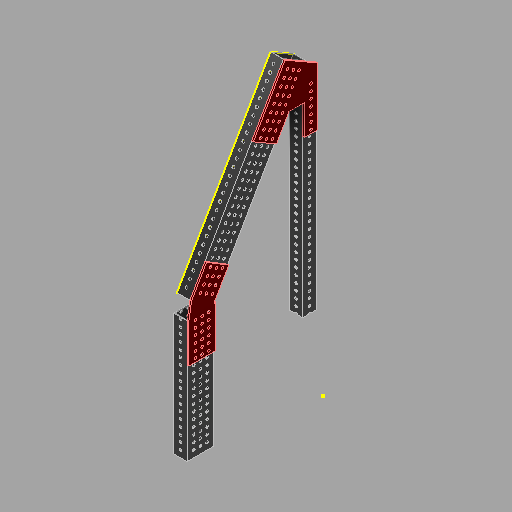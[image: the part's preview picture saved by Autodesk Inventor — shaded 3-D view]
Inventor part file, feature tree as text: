
AUTODESK INVENTOR PART (.ipt)
format: ipt  version: 2024.2 (Build 282272000, 272)  size: 1,339,904 bytes
history: native  units: in
note: dims shown in document units (in); Inventor stores cm internally (conversion verified against a paired STEP export)
features: extrude x12, projected_geometry x11, sketch x10, other x5
ambient origin geometry x8: Origin, YZ Plane, XZ Plane, XY Plane, X Axis, Y Axis, Z Axis, Center Point
bodies: Body1 (feature_tree), Body2 (feature_tree), Body3 (feature_tree), Body4 (feature_tree), Body5 (feature_tree)
feature tree (38):
  other  "2024-210-001-Shooter-Beam"
  sketch  "Sketch1"  dims[d25=9.12in d26=2.0in]
  extrude  "Extrusion1"  Depth=2.0in
  extrude  "Extrusion2"  Depth=2.0in
  extrude  "Extrusion3"  TaperAngle=60.0deg  [1 undecoded]
  extrude  "Extrusion4"  Depth=2.0in
  extrude  "Extrusion5"  Depth=6.654in
  extrude  "Extrusion6"  Depth=2.0in
  sketch  "Sketch5"  dims[d43=1.0in d44=6.654in]
  extrude  "Extrusion7"  Depth=2.0in
  extrude  "Extrusion8"  Depth=0.5in
  extrude  "Extrusion9"  Depth=17.5in
  extrude  "Extrusion10"  Depth=1.0in TaperAngle=0.0deg
  extrude  "Extrusion12"  Depth=1.0in TaperAngle=0.0deg
  extrude  "Extrusion13"  Depth=2.0in
  sketch  "Sketch10"  dims[d71=1.0in d72=0.0in d73=1.0in d74=0.0in d85=1.0in d86=0.0in d87=0.196in d88=0.5in d89=0.5in d90=1.1811in d92=0.5in d93=7.0866in d95=0.5in d98=0.0625in d99=9.5625in d100=0.0in d101=0.0625in d102=9.5625in d103=0.0in d104=0.196in d105=0.5in d106=0.5in d107=13.7795in d109=0.5in d110=0.3937in d112=1.0in d114=0.0625in d115=1.0in d116=0.0in d117=2.87in d118=2.25in d119=2.25in d120=1.5in d122=4.75in d123=0.125in d124=0.0in d125=0.125in d126=0.0in d130=0.196in d131=0.5in d132=0.5in d133=13.7795in d135=0.5in d136=0.3937in d138=1.0in d140=0.125in d141=0.0in d142=0.196in d143=0.5in d144=0.5in d145=10.6299in d147=0.5in d148=0.3937in d150=1.0in d152=1.0in d153=0.0in d166=0.196in d167=0.5in d168=0.5in d169=7.0866in d171=0.5in d172=0.3937in d174=1.0in d176=1.0in d177=0.0in d178=2.0in d179=0.0in d127=0.5in d128=0.0344in]
  other  "2024-210-003-Front-Angle"
  other  "2024-210-002-Backright-Support"
  sketch  "Sketch2"  dims[d29=2.0in d34=0.25in]
  projected_geometry  "Projected Loop1"
  sketch  "Sketch3"  dims[d37=14.0in d39=60.0deg]
  projected_geometry  "Projected Loop2"
  sketch  "Sketch4"  dims[d41=1.0in d42=2.0in]
  projected_geometry  "Projected Loop3"
  projected_geometry  "Projected Loop4"
  projected_geometry  "Projected Loop5"
  projected_geometry  "Projected Loop6"
  other  "2024-210-004-Back-Gusset"
  other  "2024-210-005-Front-Gusset"
  sketch  "Sketch6"  dims[d45=2.0in d46=17.346in]
  projected_geometry  "Projected Loop7"
  sketch  "Sketch7"  dims[d48=0.196in d59=2.0in]
  projected_geometry  "Projected Loop8"
  sketch  "Sketch8"  dims[d60=0.5in d61=0.5in]
  projected_geometry  "Projected Loop9"
  sketch  "Sketch9"  dims[d62=1.1811in d64=0.5in d65=10.6299in d67=0.5in d70=17.5in]
  projected_geometry  "Projected Loop10"
  projected_geometry  "Projected Loop11"
note: 1 required parameter value undecoded (feature->parameter linkage not recoverable at this tier; creation-order binding heuristic only, values carry confidence <= 0.55)
